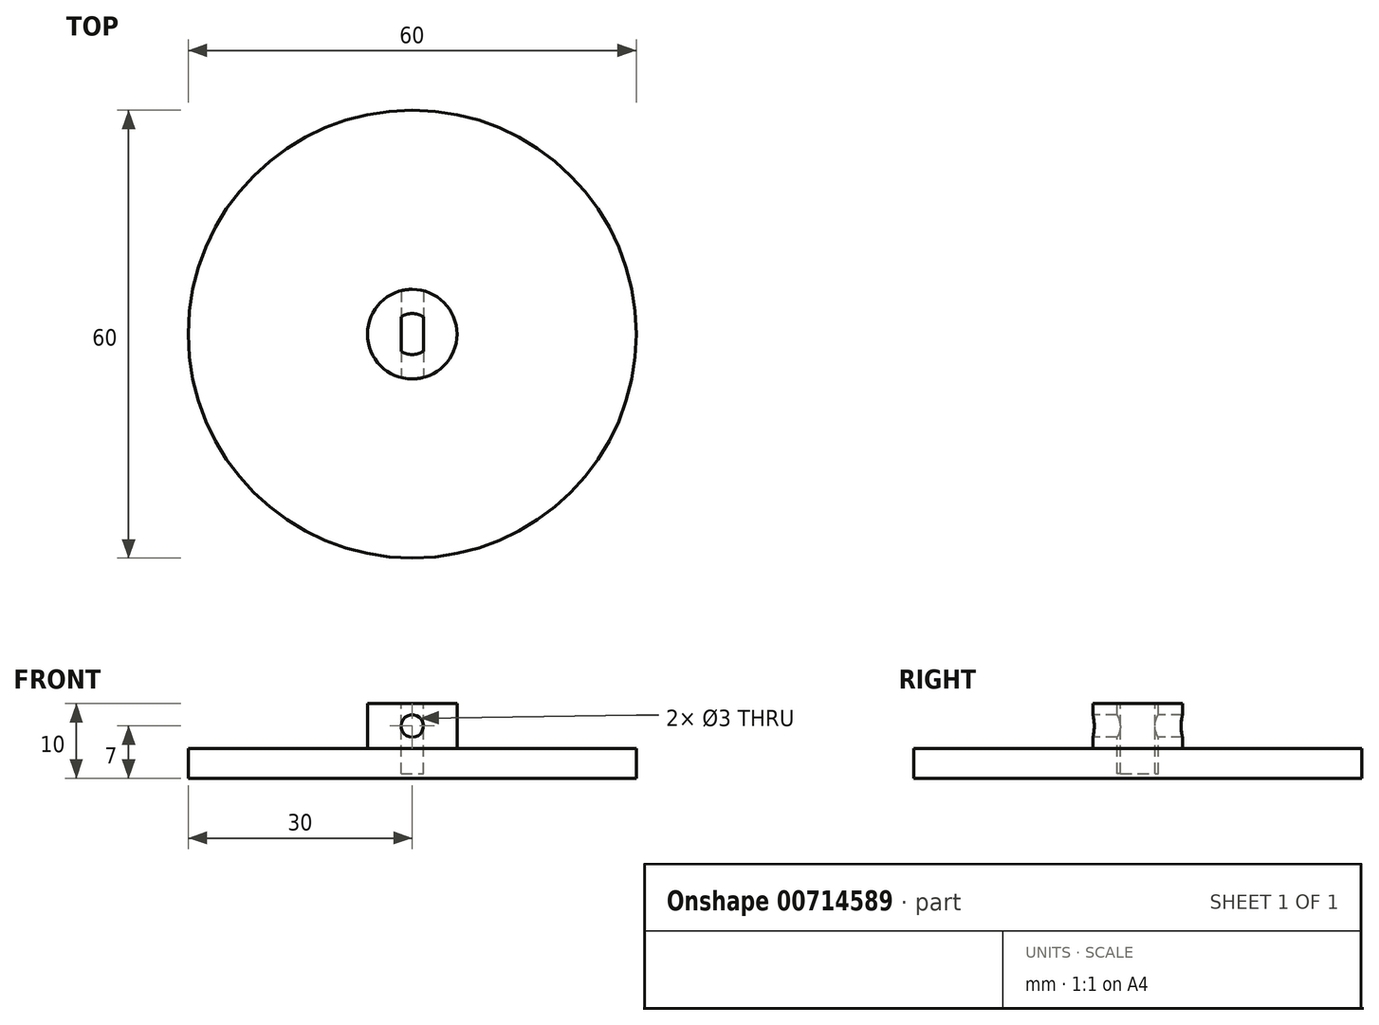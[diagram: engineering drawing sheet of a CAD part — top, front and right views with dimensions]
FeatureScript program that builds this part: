
annotation { "Feature Type Name" : "Feature", "Feature Type Description" : "" }
export const myFeature = defineFeature(function(context is Context, id is Id, definition is map)
    precondition{}
    {
        {
            var Q0;
            Q0=qCreatedBy(makeId("Top.planeOp"),FACE);
            var sketch = newSketch(context, id + "F0", { "sketchPlane" : qUnion([Q0])});
            skCircle(sketch, "E0", {"center": v(0, 0) * mm, "radius": 30 * mm});
            skSolve(sketch);
        }
        {
            var Q0;
            Q0 = qSketchRegion(id + "F0", true);
            extrude(context, id + "F1", {"entities" : qUnion([Q0]), "depth" : 4 * mm, "offsetDistance" : 25 * mm});
        }
        {
            var Q0;
            Q0=makeQuery(id+"F1.opExtrude","CAP_FACE",FACE,{"disambiguationData":[OSD([sQuery(id+"F0.wireOp",EDGE,"E0")])],"isStart":false});
            var sketch = newSketch(context, id + "F2", { "sketchPlane" : qUnion([Q0])});
            skCircle(sketch, "E1", {"center": v(0, 0) * mm, "radius": 6 * mm});
            skSolve(sketch);
        }
        {
            var Q0;
            Q0=makeQuery(id+"F2.imprint","IMPRINT",FACE,{"disambiguationData":[TD([[makeQuery(id+"F2.imprint","IMPRINT",EDGE,{"derivedFrom":sQuery(id+"F2.wireOp",EDGE,"E1")}),1.0]])]});
            extrude(context, id + "F3", {"entities" : qUnion([Q0]), "operationType" : NewBodyOperationType.ADD, "depth" : 6 * mm, "offsetDistance" : 25 * mm});
        }
        {
            var Q0;
            Q0=qCreatedBy(makeId("Front.planeOp"),FACE);
            var sketch = newSketch(context, id + "F4", { "sketchPlane" : qUnion([Q0])});
            skCircle(sketch, "E2", {"center": v(0, 7) * mm, "radius": 1.5 * mm});
            skSolve(sketch);
        }
        {
            var Q0;
            Q0 = qSketchRegion(id + "F4", true);
            extrude(context, id + "F5", {"entities" : qUnion([Q0]), "operationType" : NewBodyOperationType.REMOVE, "endBound" : BoundingType.SYMMETRIC, "oppositeDirection" : true, "depth" : 25 * mm, "offsetDistance" : 25 * mm});
        }
        {
            var Q0;
            Q0=makeQuery(id+"F3.opExtrude","CAP_FACE",FACE,{"disambiguationData":[OSD([sQuery(id+"F2.wireOp",EDGE,"E1")])],"isStart":false});
            var sketch = newSketch(context, id + "F6", { "sketchPlane" : qUnion([Q0])});
            skLineSegment(sketch, "E3.bottom", {"start": v(1.5, -2.3) * mm, "end": v(-1.5, -2.3) * mm});
            skLineSegment(sketch, "E3.top", {"start": v(1.5, 2.3) * mm, "end": v(-1.5, 2.3) * mm});
            skLineSegment(sketch, "E3.left", {"start": v(1.5, -2.3) * mm, "end": v(1.5, 2.3) * mm});
            skLineSegment(sketch, "E3.right", {"start": v(-1.5, -2.3) * mm, "end": v(-1.5, 2.3) * mm});
            skPoint(sketch, "E3.middle", {"position": v(0, 0) * mm});
            skArc(sketch, "E4", {"start": v(1.5, 2.3) * mm, "mid": v(0, 2.75) * mm, "end": v(-1.5, 2.3) * mm});
            skArc(sketch, "E5", {"start": v(-1.5, -2.3) * mm, "mid": v(0, -2.75) * mm, "end": v(1.5, -2.3) * mm});
            skSolve(sketch);
        }
        {
            var Q0;
            Q0 = qSketchRegion(id + "F6", true);
            extrude(context, id + "F7", {"entities" : qUnion([Q0]), "operationType" : NewBodyOperationType.REMOVE, "oppositeDirection" : true, "depth" : 9.4 * mm, "offsetDistance" : 25 * mm});
        }
    });
